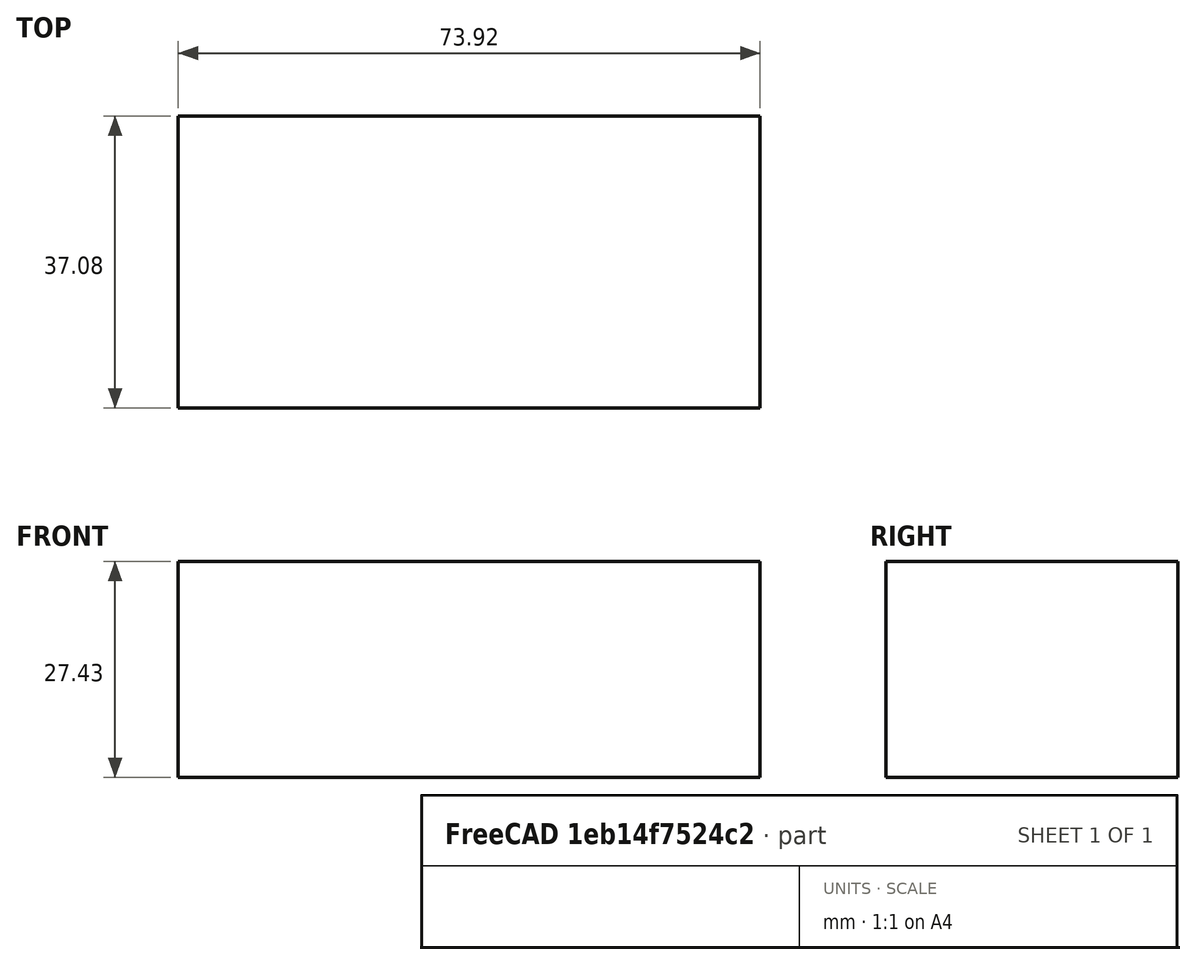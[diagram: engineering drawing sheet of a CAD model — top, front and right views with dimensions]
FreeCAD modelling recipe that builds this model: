
FCSTD DOCUMENT  (FreeCAD 0.15R4671 (Git))
Label: Floureon_3s_1500mAh_battery
License: All rights reserved
LicenseURL: http://en.wikipedia.org/wiki/All_rights_reserved
objects: Sketcher::SketchObject×1, PartDesign::Pad×1
note: 3 computed .brp shape members not serialized (recipe doc carries the construction recipe); baked Part::Feature solids carry a one-line shape summary decoded from their .brp

FEATURE [Sketcher::SketchObject] Sketch
  sketch-geometry (4):
    g0: LineSegment StartX=-36.957 StartY=18.542 StartZ=0 EndX=36.957 EndY=18.542 EndZ=0
    g1: LineSegment StartX=36.957 StartY=18.542 StartZ=0 EndX=36.957 EndY=-18.542 EndZ=0
    g2: LineSegment StartX=36.957 StartY=-18.542 StartZ=0 EndX=-36.957 EndY=-18.542 EndZ=0
    g3: LineSegment StartX=-36.957 StartY=-18.542 StartZ=0 EndX=-36.957 EndY=18.542 EndZ=0
  constraints (11):
    c: Coincident(g0,g1)
    c: Coincident(g1,g2)
    c: Coincident(g2,g3)
    c: Coincident(g3,g0)
    c: Horizontal(g0)
    c: Horizontal(g2)
    c: Vertical(g1)
    c: Vertical(g3)
    c: DistanceX(g0) = 73.914
    c: DistanceY(g3) = 37.084
    c: Symmetric(g0,g1,g-1)
FEATURE [PartDesign::Pad] Pad
  Length = 27.432
  Length2 = 100
  Sketch = -> Sketch
  Type = 0
